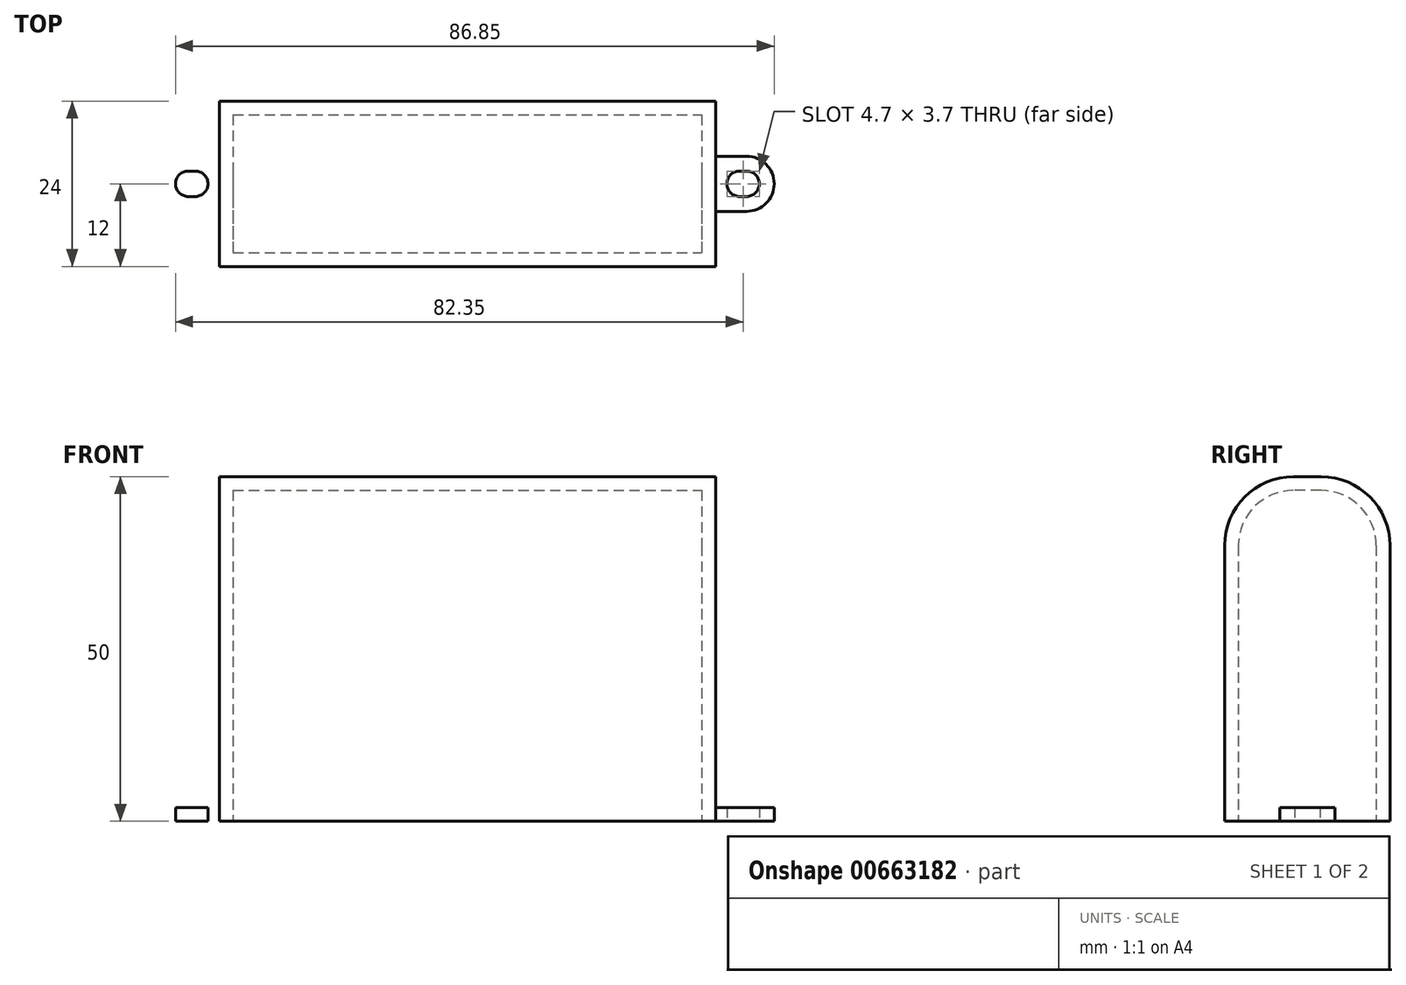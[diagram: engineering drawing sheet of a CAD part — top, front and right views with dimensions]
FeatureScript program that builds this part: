
annotation { "Feature Type Name" : "Feature", "Feature Type Description" : "" }
export const myFeature = defineFeature(function(context is Context, id is Id, definition is map)
    precondition{}
    {
        {
            var Q0;
            Q0=qCreatedBy(makeId("Top.planeOp"),FACE);
            var sketch = newSketch(context, id + "F0", { "sketchPlane" : qUnion([Q0])});
            skLineSegment(sketch, "E0.bottom", {"start": v(-36, 12) * mm, "end": v(36, 12) * mm});
            skLineSegment(sketch, "E0.top", {"start": v(-36, -12) * mm, "end": v(36, -12) * mm});
            skLineSegment(sketch, "E0.left", {"start": v(-36, 12) * mm, "end": v(-36, -12) * mm});
            skLineSegment(sketch, "E0.right", {"start": v(36, 12) * mm, "end": v(36, -12) * mm});
            skLineSegment(sketch, "E1", {"start": v(-40.5, 0) * mm, "end": v(-39.5, 0) * mm, "construction": true});
            skArc(sketch, "E2.0.startCap", {"start": v(-40.5, -1.85) * mm, "mid": v(-42.35, 0) * mm, "end": v(-40.5, 1.85) * mm});
            skArc(sketch, "E2.0.endCap", {"start": v(-39.5, 1.85) * mm, "mid": v(-37.65, 0) * mm, "end": v(-39.5, -1.85) * mm});
            skLineSegment(sketch, "E2.0.left", {"start": v(-40.5, 1.85) * mm, "end": v(-39.5, 1.85) * mm});
            skLineSegment(sketch, "E2.0.right", {"start": v(-40.5, -1.85) * mm, "end": v(-39.5, -1.85) * mm});
            skLineSegment(sketch, "E3", {"start": v(-40.5, 4) * mm, "end": v(-36, 4) * mm});
            skLineSegment(sketch, "E4", {"start": v(-40.5, -4) * mm, "end": v(-36, -4) * mm});
            skArc(sketch, "E5", {"start": v(-40.5, 4) * mm, "mid": v(-44.5, 0) * mm, "end": v(-40.5, -4) * mm});
            skPoint(sketch, "E6", {"position": v(-40, 0) * mm});
            skLineSegment(sketch, "E7.MirrorCS", {"start": v(40.5, -1.85) * mm, "end": v(39.5, -1.85) * mm});
            skLineSegment(sketch, "E8.MirrorCS", {"start": v(40.5, 0) * mm, "end": v(39.5, 0) * mm, "construction": true});
            skLineSegment(sketch, "E9.MirrorCS", {"start": v(40.5, 1.85) * mm, "end": v(39.5, 1.85) * mm});
            skArc(sketch, "E10.MirrorCS", {"start": v(40.5, 4) * mm, "mid": v(44.5, 0) * mm, "end": v(40.5, -4) * mm});
            skLineSegment(sketch, "E11.MirrorCS", {"start": v(40.5, -4) * mm, "end": v(36, -4) * mm});
            skLineSegment(sketch, "E12.MirrorCS", {"start": v(40.5, 4) * mm, "end": v(36, 4) * mm});
            skArc(sketch, "E13.MirrorCS", {"start": v(39.5, 1.85) * mm, "mid": v(37.65, 0) * mm, "end": v(39.5, -1.85) * mm});
            skArc(sketch, "E14.MirrorCS", {"start": v(40.5, -1.85) * mm, "mid": v(42.35, 0) * mm, "end": v(40.5, 1.85) * mm});
            skPoint(sketch, "E15.MirrorP", {"position": v(40, 0) * mm});
            skSolve(sketch);
        }
        {
            var Q0;
            {var subQ3=sQuery(id+"F0.wireOp",EDGE,"E0.bottom");Q0=makeQuery(id+"F0.imprint","IMPRINT",FACE,{"disambiguationData":[TD([[makeQuery(id+"F0.imprint","IMPRINT",EDGE,{"derivedFrom":subQ3}),-1.0]])]});}
            extrude(context, id + "F1", {"entities" : qUnion([Q0]), "depth" : 50 * mm, "offsetDistance" : 25 * mm});
        }
        {
            var Q0;
            Q0=makeQuery(id+"F1.opExtrude","CAP_EDGE",EDGE,{"disambiguationData":[OSD([sQuery(id+"F0.wireOp",EDGE,"E0.top")])],"isStart":false});
            var Q1;
            Q1=makeQuery(id+"F1.opExtrude","CAP_EDGE",EDGE,{"disambiguationData":[OSD([sQuery(id+"F0.wireOp",EDGE,"E0.bottom")])],"isStart":false});
            fillet(context, id + "F2", {"entities" : qUnion([Q0, Q1]), "radius" : 10 * mm, "tangentPropagation" : true, "allowEdgeOverflow" : false});
        }
        {
            var Q0;
            {var subQ0=sQuery(id+"F0.wireOp",EDGE,"E0.right");var subQ1=sQuery(id+"F0.wireOp",EDGE,"E0.left");Q0=makeQuery(id+"F4.boolean.opBoolean","MERGE",FACE,{"derivedFrom":[makeQuery(id+"F1.opExtrude","CAP_FACE",FACE,{"disambiguationData":[OSD([sQuery(id+"F0.wireOp",EDGE,"E0.bottom"),sQuery(id+"F0.wireOp",EDGE,"E0.top"),subQ1,subQ0])],"isStart":true}),makeQuery(id+"F4.opExtrude","CAP_FACE",FACE,{"disambiguationData":[OSD([subQ1,sQuery(id+"F0.wireOp",EDGE,"E2.0.startCap"),sQuery(id+"F0.wireOp",EDGE,"E2.0.endCap"),sQuery(id+"F0.wireOp",EDGE,"E2.0.left"),sQuery(id+"F0.wireOp",EDGE,"E2.0.right"),sQuery(id+"F0.wireOp",EDGE,"E3"),sQuery(id+"F0.wireOp",EDGE,"E4"),sQuery(id+"F0.wireOp",EDGE,"E5")])],"isStart":true}),makeQuery(id+"F4.opExtrude","CAP_FACE",FACE,{"disambiguationData":[OSD([subQ0,sQuery(id+"F0.wireOp",EDGE,"E7.MirrorCS"),sQuery(id+"F0.wireOp",EDGE,"E9.MirrorCS"),sQuery(id+"F0.wireOp",EDGE,"E10.MirrorCS"),sQuery(id+"F0.wireOp",EDGE,"E11.MirrorCS"),sQuery(id+"F0.wireOp",EDGE,"E12.MirrorCS"),sQuery(id+"F0.wireOp",EDGE,"E13.MirrorCS"),sQuery(id+"F0.wireOp",EDGE,"E14.MirrorCS")])],"isStart":true})]});}
            shell(context, id + "F3", {"entities" : qUnion([Q0]), "thickness" : 2 * mm});
        }
        {
            var Q0;
            Q0=makeQuery(id+"F0.imprint","IMPRINT",FACE,{"disambiguationData":[TD([[makeQuery(id+"F0.imprint","IMPRINT",EDGE,{"derivedFrom":sQuery(id+"F0.wireOp",EDGE,"E2.0.startCap")}),1.0]])]});
            var Q1;
            Q1=makeQuery(id+"F0.imprint","IMPRINT",FACE,{"disambiguationData":[TD([[makeQuery(id+"F0.imprint","IMPRINT",EDGE,{"derivedFrom":sQuery(id+"F0.wireOp",EDGE,"E7.MirrorCS")}),1.0]])]});
            extrude(context, id + "F4", {"entities" : qUnion([Q0, Q1]), "operationType" : NewBodyOperationType.ADD, "depth" : 2 * mm, "offsetDistance" : 25 * mm});
        }
    });
